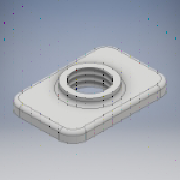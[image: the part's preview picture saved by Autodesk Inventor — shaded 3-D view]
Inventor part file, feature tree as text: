
AUTODESK INVENTOR PART (.ipt)
format: ipt  version: 2017 (Build 210142000, 142)  size: 175,616 bytes
history: native  units: mm
features: extrude x2, fillet x2, sketch x2, thread x1
ambient origin geometry x8: Origin, YZ Plane, XZ Plane, XY Plane, X Axis, Y Axis, Z Axis, Center Point
bodies: Solid1 (feature_tree)
feature tree (7):
  extrude  "Extrusion1"  Depth=15.0mm
  extrude  "Extrusion2"  Depth=2.0mm
  fillet  "Fillet1"  Radius=1.5mm
  thread  "Thread1"  [1 undecoded]
  fillet  "Fillet2"  Radius=1.0mm
  sketch  "Sketch1"  dims[d0=10.0mm d1=15.0mm]
  sketch  "Sketch2"  dims[d2=4.8mm d3=2.0mm d4=1.5mm d5=0.0mm d6=6.5mm d7=1.0mm d8=0.0mm d9=0.5mm d10=10.0mm d11=0.0mm d12=0.5mm]
note: 1 required parameter value undecoded (feature->parameter linkage not recoverable at this tier; creation-order binding heuristic only, values carry confidence <= 0.55)
